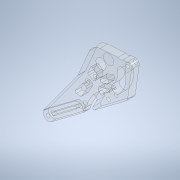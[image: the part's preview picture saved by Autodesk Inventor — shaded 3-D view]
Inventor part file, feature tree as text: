
AUTODESK INVENTOR PART (.ipt)
format: ipt  version: 2020.2 (Build 242310000, 310)  size: 732,160 bytes
history: native  units: mm
features: sketch x17, extrude x12, projected_geometry x11, other x3, hole x2, fillet x2
ambient origin geometry x8: Origin, YZ Plane, XZ Plane, XY Plane, X Axis, Y Axis, Z Axis, Center Point
bodies: Body1 (feature_tree)
feature tree (47):
  other  "ソリッド1"
  sketch  "スケッチ1"
  sketch  "スケッチ2"
  extrude  "押し出し1"  Depth=5.0mm TaperAngle=0.0deg
  hole  "穴1"  [1 undecoded]
  fillet  "フィレット1"  Radius=4.0mm
  extrude  "押し出し2"  Depth=5.0mm TaperAngle=0.0deg
  extrude  "押し出し3"  Depth=10.0mm TaperAngle=0.0deg
  extrude  "押し出し4"  Depth=1.0mm TaperAngle=0.0deg
  extrude  "押し出し5"  Depth=4.014257mm
  sketch  "スケッチ7"
  extrude  "押し出し6"  Depth=7.971681mm
  extrude  "押し出し7"  Depth=3.98584mm
  extrude  "押し出し8"  Depth=2.0mm TaperAngle=0.0deg
  sketch  "スケッチ9"
  extrude  "押し出し9"  Depth=4.0mm TaperAngle=0.0deg
  hole  "穴2"  [1 undecoded]
  sketch  "スケッチ10"
  extrude  "押し出し10"  Depth=6.5mm
  sketch  "スケッチ12"
  extrude  "押し出し11"  Depth=10.0mm TaperAngle=0.0deg
  extrude  "押し出し12"  Depth=7.0mm
  sketch  "スケッチ13"
  sketch  "スケッチ14"
  sketch  "スケッチ15"
  fillet  "フィレット2"  Radius=6.0mm
  sketch  "スケッチ16"
  sketch  "スケッチ17"
  sketch  "スケッチ3"
  projected_geometry  "投影ループ1"
  sketch  "スケッチ4"
  projected_geometry  "投影ループ2"
  sketch  "スケッチ5"
  projected_geometry  "投影ループ3"
  sketch  "スケッチ6"
  projected_geometry  "投影ループ4"
  projected_geometry  "投影ループ5"
  sketch  "スケッチ8"
  projected_geometry  "投影ループ6"
  sketch  "スケッチ11"
  projected_geometry  "投影ループ7"
  projected_geometry  "投影ループ8"
  projected_geometry  "投影ループ9"
  projected_geometry  "投影ループ10"
  projected_geometry  "投影ループ11"
  other  "断面エッジを投影1"
  other  "断面エッジを投影2"
note: 2 required parameter values undecoded (feature->parameter linkage not recoverable at this tier; creation-order binding heuristic only, values carry confidence <= 0.55)
